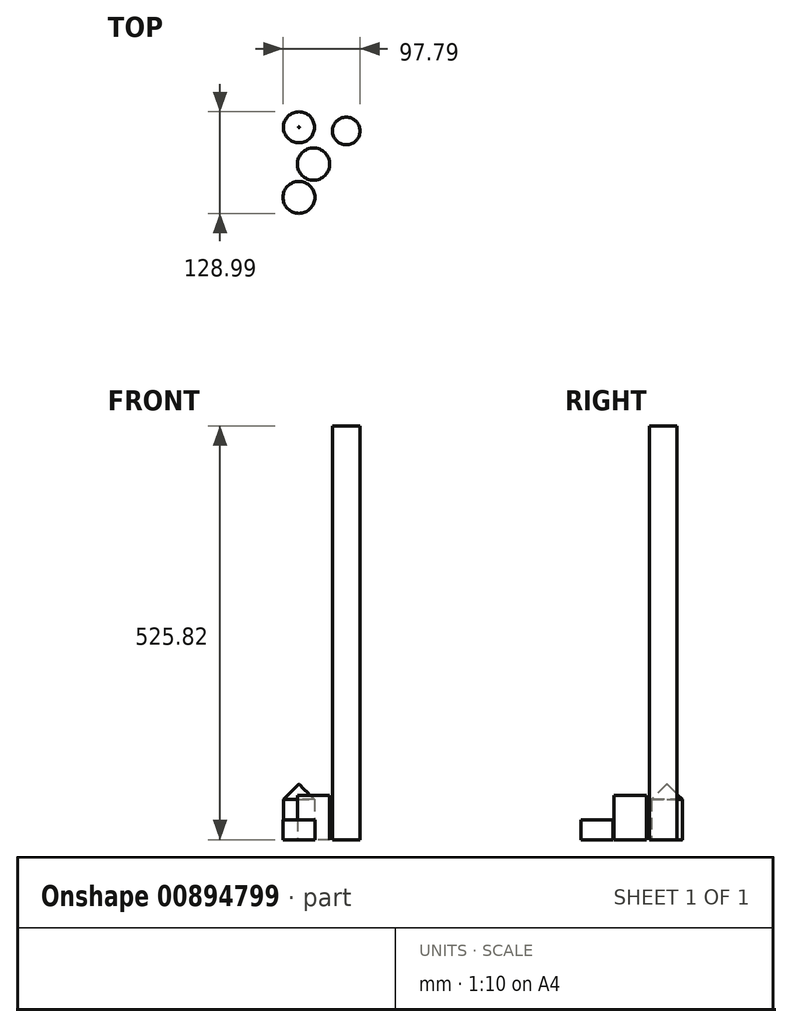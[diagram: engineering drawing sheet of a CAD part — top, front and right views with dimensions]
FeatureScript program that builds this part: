
annotation { "Feature Type Name" : "Feature", "Feature Type Description" : "" }
export const myFeature = defineFeature(function(context is Context, id is Id, definition is map)
    precondition{}
    {
        {
            var Q0;
            Q0=qCreatedBy(makeId("Top.planeOp"),FACE);
            var sketch = newSketch(context, id + "F0", { "sketchPlane" : qUnion([Q0])});
            skCircle(sketch, "E0", {"center": v(18.5, 0) * mm, "radius": 20.43 * mm});
            skSolve(sketch);
        }
        {
            var Q0;
            Q0=makeQuery(id+"F0.imprint","IMPRINT",FACE,{"disambiguationData":[TD([[makeQuery(id+"F0.imprint","IMPRINT",EDGE,{"derivedFrom":sQuery(id+"F0.wireOp",EDGE,"E0")}),1.0]])]});
            extrude(context, id + "F1", {"entities" : qUnion([Q0]), "depth" : 56.52 * mm, "offsetDistance" : 25.4 * mm});
        }
        {
            var Q0;
            Q0=qCreatedBy(makeId("Top.planeOp"),FACE);
            var sketch = newSketch(context, id + "F2", { "sketchPlane" : qUnion([Q0])});
            skCircle(sketch, "E1", {"center": v(-46.97, 0) * mm, "radius": 23.46 * mm});
            skSolve(sketch);
        }
        {
            var Q0;
            Q0=sQuery(id+"F2.wireOp",EDGE,"E1");
            extrude(context, id + "F3", {"bodyType" : ToolBodyType.SURFACE, "surfaceEntities" : qUnion([Q0]), "depth" : 529.8 * mm, "offsetDistance" : 25.4 * mm});
        }
        {
            var Q0;
            Q0=qCreatedBy(makeId("Top.planeOp"),FACE);
            var sketch = newSketch(context, id + "F4", { "sketchPlane" : qUnion([Q0])});
            skCircle(sketch, "E2", {"center": v(0, 46.77) * mm, "radius": 19.67 * mm});
            skSolve(sketch);
        }
        {
            var Q0;
            Q0=makeQuery(id+"F4.imprint","IMPRINT",FACE,{"disambiguationData":[TD([[makeQuery(id+"F4.imprint","IMPRINT",EDGE,{"derivedFrom":sQuery(id+"F4.wireOp",EDGE,"E2")}),1.0]])]});
            extrude(context, id + "F5", {"entities" : qUnion([Q0]), "depth" : 70.1 * mm, "offsetDistance" : 25.4 * mm});
        }
        {
            var Q0;
            Q0=makeQuery(id+"F5.opExtrude","CAP_EDGE",EDGE,{"disambiguationData":[OSD([sQuery(id+"F4.wireOp",EDGE,"E2")])],"isStart":false});
            chamfer(context, id + "F6", {"entities" : qUnion([Q0]), "width" : 19.05 * mm, "tangentPropagation" : true});
        }
        {
            var Q0;
            Q0=qCreatedBy(makeId("Top.planeOp"),FACE);
            var sketch = newSketch(context, id + "F7", { "sketchPlane" : qUnion([Q0])});
            skCircle(sketch, "E3", {"center": v(0, -42.3) * mm, "radius": 20.25 * mm});
            skSolve(sketch);
        }
        {
            var Q0;
            Q0=makeQuery(id+"F7.imprint","IMPRINT",FACE,{"disambiguationData":[TD([[makeQuery(id+"F7.imprint","IMPRINT",EDGE,{"derivedFrom":sQuery(id+"F7.wireOp",EDGE,"E3")}),1.0]])]});
            extrude(context, id + "F8", {"entities" : qUnion([Q0]), "depth" : 25.4 * mm, "offsetDistance" : 25.4 * mm});
        }
        {
            var Q0;
            Q0=qCreatedBy(makeId("Top.planeOp"),FACE);
            var sketch = newSketch(context, id + "F9", { "sketchPlane" : qUnion([Q0])});
            skCircle(sketch, "E4", {"center": v(60.04, 42.07) * mm, "radius": 17.5 * mm});
            skSolve(sketch);
        }
        {
            var Q0;
            Q0=makeQuery(id+"F9.imprint","IMPRINT",FACE,{"disambiguationData":[TD([[makeQuery(id+"F9.imprint","IMPRINT",EDGE,{"derivedFrom":sQuery(id+"F9.wireOp",EDGE,"E4")}),1.0]])]});
            extrude(context, id + "F10", {"entities" : qUnion([Q0]), "depth" : 525.82 * mm, "offsetDistance" : 25.4 * mm});
        }
    });
